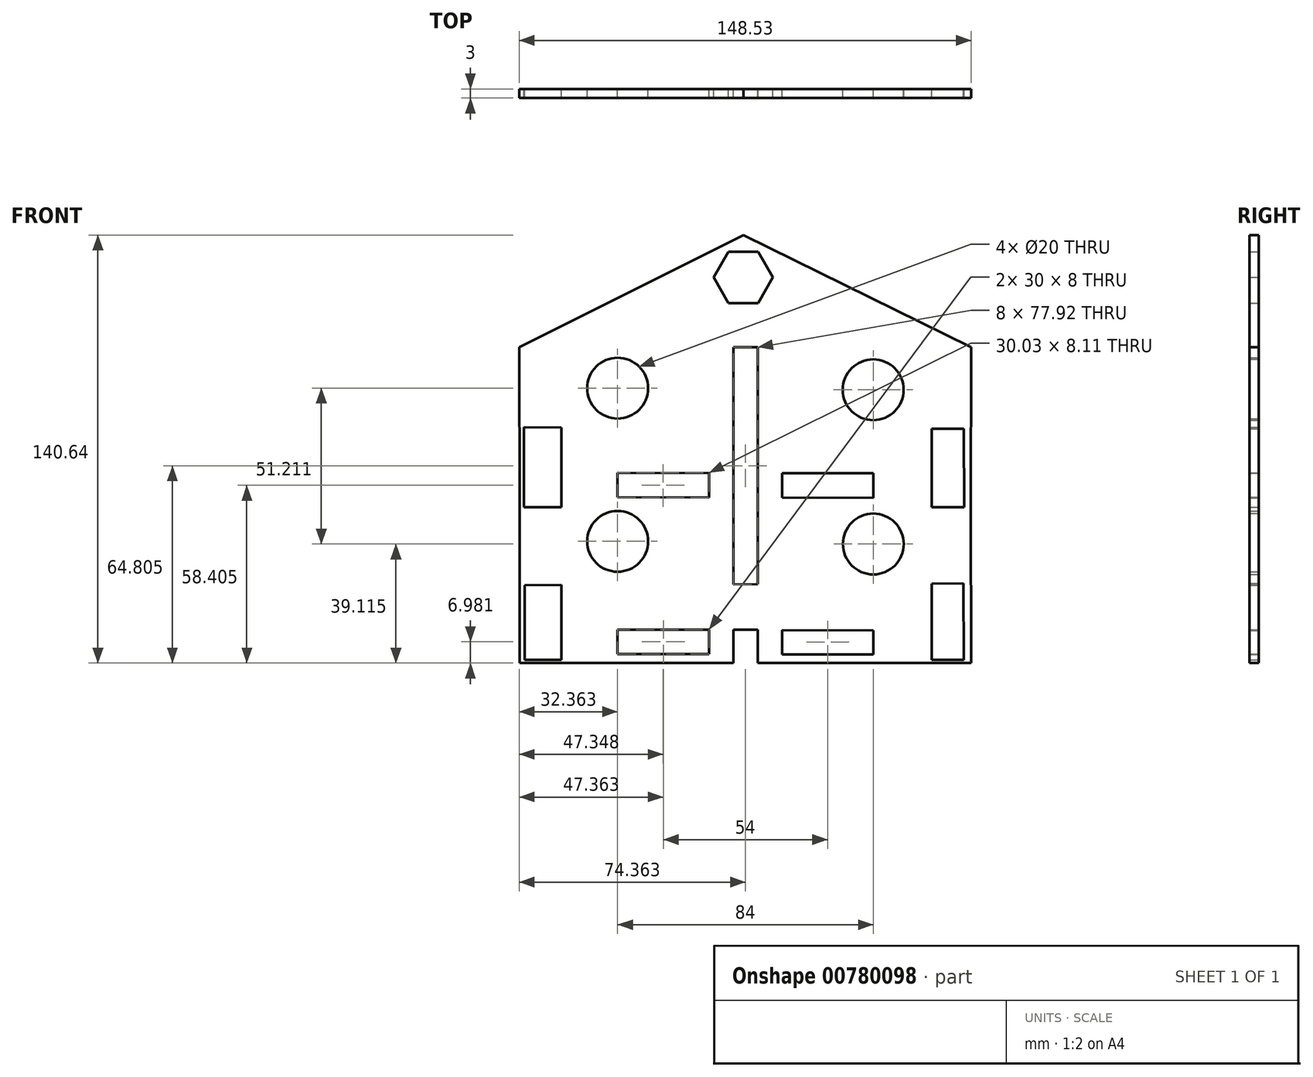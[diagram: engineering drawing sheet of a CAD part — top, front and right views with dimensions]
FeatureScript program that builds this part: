
annotation { "Feature Type Name" : "Feature", "Feature Type Description" : "" }
export const myFeature = defineFeature(function(context is Context, id is Id, definition is map)
    precondition{}
    {
        {
            var Q0;
            Q0=qCreatedBy(makeId("Front.planeOp"),FACE);
            var sketch = newSketch(context, id + "F0", { "sketchPlane" : qUnion([Q0])});
            skLineSegment(sketch, "E0", {"start": v(-73.48, -51.17) * mm, "end": v(74.85, -51.17) * mm});
            skLineSegment(sketch, "E1", {"start": v(-73.48, -51.17) * mm, "end": v(-73.48, 0) * mm});
            skLineSegment(sketch, "E2", {"start": v(-73.48, 0) * mm, "end": v(74.66, 0) * mm});
            skLineSegment(sketch, "E3", {"start": v(74.66, 0) * mm, "end": v(74.85, -51.17) * mm});
            skLineSegment(sketch, "E4", {"start": v(-73.48, 0) * mm, "end": v(-73.68, 52.6) * mm});
            skLineSegment(sketch, "E5", {"start": v(-73.68, 52.6) * mm, "end": v(74.85, 52.6) * mm});
            skLineSegment(sketch, "E6", {"start": v(74.85, 52.6) * mm, "end": v(74.66, 0) * mm});
            skLineSegment(sketch, "E7", {"start": v(-73.68, 52.6) * mm, "end": v(0, 89.47) * mm});
            skLineSegment(sketch, "E8", {"start": v(0, 89.47) * mm, "end": v(74.85, 52.6) * mm});
            skLineSegment(sketch, "E9", {"start": v(-73.48, -25.58) * mm, "end": v(74.76, -25.03) * mm});
            skPoint(sketch, "E9.endSnap0", {"position": v(74.76, -25.58) * mm});
            skLineSegment(sketch, "E10", {"start": v(-73.58, 26.3) * mm, "end": v(74.76, 25.76) * mm});
            skPoint(sketch, "E10.endSnap0", {"position": v(74.76, 26.3) * mm});
            skLineSegment(sketch, "E11", {"start": v(0.68, -51.17) * mm, "end": v(-3.32, -51.17) * mm});
            skLineSegment(sketch, "E12", {"start": v(0.68, -51.17) * mm, "end": v(4.68, -51.17) * mm});
            skLineSegment(sketch, "E13", {"start": v(-3.32, -51.17) * mm, "end": v(-3.32, -40.17) * mm});
            skLineSegment(sketch, "E14", {"start": v(4.68, -51.17) * mm, "end": v(4.68, -40.17) * mm});
            skLineSegment(sketch, "E15", {"start": v(-3.32, -40.17) * mm, "end": v(4.68, -40.17) * mm});
            skLineSegment(sketch, "E16", {"start": v(12.68, -40.31) * mm, "end": v(42.68, -40.42) * mm});
            skLineSegment(sketch, "E17", {"start": v(12.68, -40.31) * mm, "end": v(12.68, -48.31) * mm});
            skLineSegment(sketch, "E18", {"start": v(12.68, -48.31) * mm, "end": v(42.68, -48.31) * mm});
            skLineSegment(sketch, "E19", {"start": v(42.68, -40.42) * mm, "end": v(42.68, -48.31) * mm});
            skLineSegment(sketch, "E20", {"start": v(-11.32, -40.19) * mm, "end": v(-41.32, -40.19) * mm});
            skLineSegment(sketch, "E21", {"start": v(-41.32, -40.19) * mm, "end": v(-41.32, -48.19) * mm});
            skLineSegment(sketch, "E22", {"start": v(-41.32, -48.19) * mm, "end": v(-11.32, -48.19) * mm});
            skLineSegment(sketch, "E23", {"start": v(-11.32, -40.19) * mm, "end": v(-11.32, -48.19) * mm});
            skLineSegment(sketch, "E24", {"start": v(-59.74, -25.53) * mm, "end": v(-59.74, -51.17) * mm});
            skLineSegment(sketch, "E25", {"start": v(61.84, -51.17) * mm, "end": v(61.93, -25.08) * mm});
            skLineSegment(sketch, "E26", {"start": v(-3.32, -25.32) * mm, "end": v(-3.32, 52.6) * mm});
            skLineSegment(sketch, "E27", {"start": v(4.68, -25.3) * mm, "end": v(4.68, 52.6) * mm});
            skLineSegment(sketch, "E28", {"start": v(61.93, 0) * mm, "end": v(61.83, 25.8) * mm});
            skLineSegment(sketch, "E29", {"start": v(-59.74, 0) * mm, "end": v(-59.84, 26.25) * mm});
            skLineSegment(sketch, "E30", {"start": v(-11.32, 3.18) * mm, "end": v(-41.32, 3.29) * mm});
            skLineSegment(sketch, "E31", {"start": v(-41.32, 3.29) * mm, "end": v(-41.35, 11.29) * mm});
            skLineSegment(sketch, "E32", {"start": v(-41.35, 11.29) * mm, "end": v(-11.32, 11.18) * mm});
            skLineSegment(sketch, "E33", {"start": v(-11.32, 11.18) * mm, "end": v(-11.32, 3.18) * mm});
            skLineSegment(sketch, "E34", {"start": v(12.68, 3.18) * mm, "end": v(42.68, 3.07) * mm});
            skLineSegment(sketch, "E35", {"start": v(42.68, 3.07) * mm, "end": v(42.65, 11.18) * mm});
            skLineSegment(sketch, "E36", {"start": v(42.65, 11.18) * mm, "end": v(12.68, 11.18) * mm});
            skLineSegment(sketch, "E37", {"start": v(12.68, 11.18) * mm, "end": v(12.68, 3.18) * mm});
            skCircle(sketch, "E38", {"center": v(-41.32, -11.18) * mm, "radius": 10 * mm});
            skCircle(sketch, "E39", {"center": v(42.68, -12.05) * mm, "radius": 10 * mm});
            skCircle(sketch, "E40", {"center": v(42.65, 38.63) * mm, "radius": 10 * mm});
            skCircle(sketch, "E41", {"center": v(-41.32, 39.16) * mm, "radius": 10 * mm});
            skCircle(sketch, "E42.cCircle", {"center": v(0, 75.56) * mm, "radius": 8.43 * mm, "construction": true});
            skLineSegment(sketch, "E42.0", {"start": v(4.87, 67.13) * mm, "end": v(-4.87, 67.13) * mm});
            skLineSegment(sketch, "E42.1", {"start": v(-4.87, 67.13) * mm, "end": v(-9.74, 75.56) * mm});
            skLineSegment(sketch, "E42.2", {"start": v(-9.74, 75.56) * mm, "end": v(-4.87, 84) * mm});
            skLineSegment(sketch, "E42.3", {"start": v(-4.87, 84) * mm, "end": v(4.87, 84) * mm});
            skLineSegment(sketch, "E42.4", {"start": v(4.87, 84) * mm, "end": v(9.74, 75.56) * mm});
            skLineSegment(sketch, "E42.5", {"start": v(9.74, 75.56) * mm, "end": v(4.87, 67.13) * mm});
            skPoint(sketch, "E42.0.midPoint", {"position": v(0, 67.13) * mm});
            skLineSegment(sketch, "E43", {"start": v(-72.12, 26.3) * mm, "end": v(-72.12, 0) * mm});
            skLineSegment(sketch, "E44", {"start": v(-71.84, -25.58) * mm, "end": v(-71.84, -51.17) * mm});
            skLineSegment(sketch, "E45", {"start": v(72.3, -25.04) * mm, "end": v(72.4, -51.17) * mm});
            skLineSegment(sketch, "E46", {"start": v(72.45, 25.77) * mm, "end": v(72.55, 0) * mm});
            skLineSegment(sketch, "E47", {"start": v(-71.84, -50.06) * mm, "end": v(-59.74, -50.06) * mm});
            skLineSegment(sketch, "E48", {"start": v(61.84, -50.12) * mm, "end": v(72.4, -50.12) * mm});
            skSolve(sketch);
        }
        {
            var Q0;
            {var subQ1=sQuery(id+"F0.wireOp",EDGE,"E7");Q0=makeQuery(id+"F0.imprint","IMPRINT",FACE,{"disambiguationData":[TD([[makeQuery(id+"F0.imprint","IMPRINT",EDGE,{"derivedFrom":subQ1}),-1.0]])]});}
            var Q1;
            Q1=makeQuery(id+"F0.imprint","IMPRINT",FACE,{"disambiguationData":[TD([[makeQuery(id+"F0.imprint","IMPRINT",EDGE,{"derivedFrom":sQuery(id+"F0.wireOp",EDGE,"E41")}),-1.0]])]});
            var Q2;
            Q2=makeQuery(id+"F0.imprint","IMPRINT",FACE,{"disambiguationData":[TD([[makeQuery(id+"F0.imprint","IMPRINT",EDGE,{"derivedFrom":sQuery(id+"F0.wireOp",EDGE,"E40")}),-1.0]])]});
            var Q3;
            {var subQ0=sQuery(id+"F0.wireOp",EDGE,"E28");Q3=makeQuery(id+"F0.imprint","IMPRINT",FACE,{"disambiguationData":[TD([[makeQuery(id+"F0.imprint","IMPRINT",EDGE,{"derivedFrom":subQ0}),1.0]])]});}
            var Q4;
            {var subQ0=sQuery(id+"F0.wireOp",EDGE,"E29");Q4=makeQuery(id+"F0.imprint","IMPRINT",FACE,{"disambiguationData":[TD([[makeQuery(id+"F0.imprint","IMPRINT",EDGE,{"derivedFrom":subQ0}),-1.0]])]});}
            var Q5;
            Q5=makeQuery(id+"F0.imprint","IMPRINT",FACE,{"disambiguationData":[TD([[makeQuery(id+"F0.imprint","IMPRINT",EDGE,{"derivedFrom":sQuery(id+"F0.wireOp",EDGE,"E38")}),-1.0]])]});
            var Q6;
            Q6=makeQuery(id+"F0.imprint","IMPRINT",FACE,{"disambiguationData":[TD([[makeQuery(id+"F0.imprint","IMPRINT",EDGE,{"derivedFrom":sQuery(id+"F0.wireOp",EDGE,"E39")}),-1.0]])]});
            var Q7;
            {var subQ5=sQuery(id+"F0.wireOp",EDGE,"E13");Q7=makeQuery(id+"F0.imprint","IMPRINT",FACE,{"disambiguationData":[TD([[makeQuery(id+"F0.imprint","IMPRINT",EDGE,{"derivedFrom":subQ5}),1.0]])]});}
            extrude(context, id + "F1", {"entities" : qUnion([Q0, Q1, Q2, Q3, Q4, Q5, Q6, Q7]), "depth" : 3 * mm, "offsetDistance" : 25 * mm});
        }
        {
            var Q0;
            {var subQ3=sQuery(id+"F0.wireOp",EDGE,"E43");Q0=makeQuery(id+"F0.imprint","IMPRINT",FACE,{"disambiguationData":[TD([[makeQuery(id+"F0.imprint","IMPRINT",EDGE,{"derivedFrom":subQ3}),-1.0]])]});}
            var Q1;
            {var subQ3=sQuery(id+"F0.wireOp",EDGE,"E44");Q1=makeQuery(id+"F0.imprint","IMPRINT",FACE,{"disambiguationData":[TD([[makeQuery(id+"F0.imprint","IMPRINT",EDGE,{"derivedFrom":subQ3}),-1.0]])]});}
            var Q2;
            {var subQ3=sQuery(id+"F0.wireOp",EDGE,"E46");Q2=makeQuery(id+"F0.imprint","IMPRINT",FACE,{"disambiguationData":[TD([[makeQuery(id+"F0.imprint","IMPRINT",EDGE,{"derivedFrom":subQ3}),1.0]])]});}
            var Q3;
            {var subQ3=sQuery(id+"F0.wireOp",EDGE,"E45");Q3=makeQuery(id+"F0.imprint","IMPRINT",FACE,{"disambiguationData":[TD([[makeQuery(id+"F0.imprint","IMPRINT",EDGE,{"derivedFrom":subQ3}),1.0]])]});}
            extrude(context, id + "F2", {"entities" : qUnion([Q0, Q1, Q2, Q3]), "operationType" : NewBodyOperationType.ADD, "depth" : 3 * mm, "offsetDistance" : 25 * mm});
        }
        {
            var Q0;
            {var subQ5=sQuery(id+"F0.wireOp",EDGE,"E48");Q0=makeQuery(id+"F0.imprint","IMPRINT",FACE,{"disambiguationData":[TD([[makeQuery(id+"F0.imprint","IMPRINT",EDGE,{"derivedFrom":subQ5}),-1.0]])]});}
            var Q1;
            {var subQ5=sQuery(id+"F0.wireOp",EDGE,"E47");Q1=makeQuery(id+"F0.imprint","IMPRINT",FACE,{"disambiguationData":[TD([[makeQuery(id+"F0.imprint","IMPRINT",EDGE,{"derivedFrom":subQ5}),-1.0]])]});}
            extrude(context, id + "F3", {"entities" : qUnion([Q0, Q1]), "operationType" : NewBodyOperationType.ADD, "depth" : 3 * mm, "offsetDistance" : 25 * mm});
        }
    });
